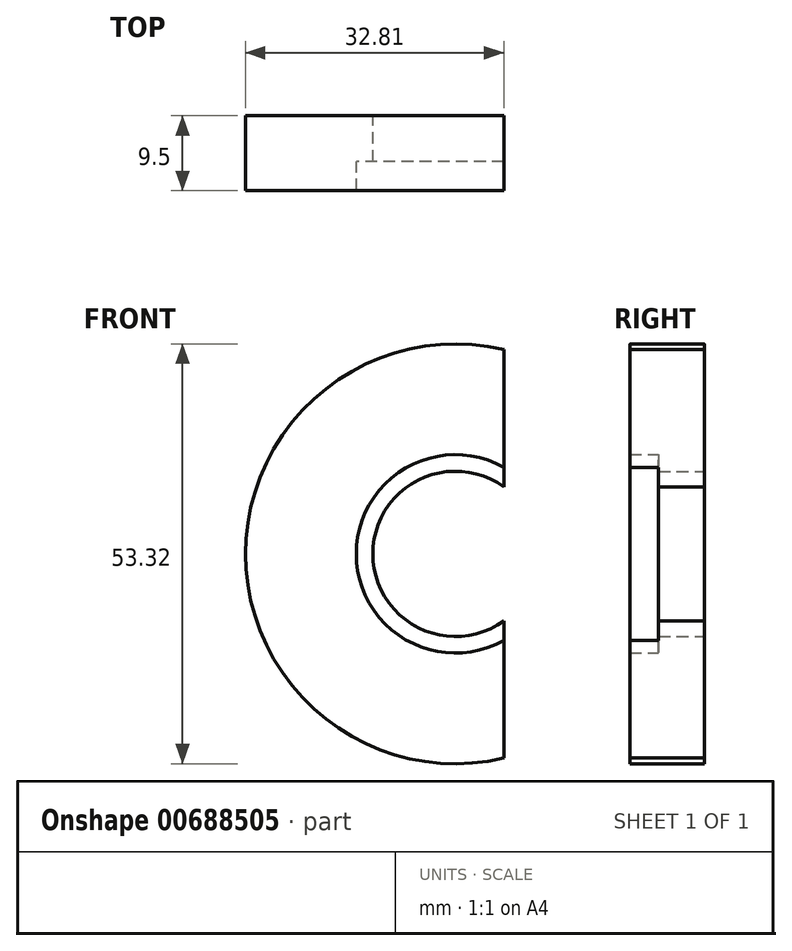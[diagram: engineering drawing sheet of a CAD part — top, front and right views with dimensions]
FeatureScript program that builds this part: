
annotation { "Feature Type Name" : "Feature", "Feature Type Description" : "" }
export const myFeature = defineFeature(function(context is Context, id is Id, definition is map)
    precondition{}
    {
        {
            var Q0;
            Q0=qCreatedBy(makeId("Top.planeOp"),FACE);
            var sketch = newSketch(context, id + "F0", { "sketchPlane" : qUnion([Q0])});
            skLineSegment(sketch, "E0", {"start": v(-57.3, 26.1) * mm, "end": v(-46.8, 26.1) * mm});
            skLineSegment(sketch, "E1", {"start": v(-57.3, 20.25) * mm, "end": v(-59.4, 20.25) * mm});
            skLineSegment(sketch, "E2", {"start": v(-59.4, 20.25) * mm, "end": v(-59.4, 16.6) * mm});
            skLineSegment(sketch, "E3", {"start": v(-46.8, 16.6) * mm, "end": v(-46.8, 10.1) * mm});
            skLineSegment(sketch, "E4", {"start": v(-65.35, 10.1) * mm, "end": v(-65.35, 16.6) * mm});
            skLineSegment(sketch, "E5", {"start": v(-65.35, 16.6) * mm, "end": v(-59.4, 16.6) * mm});
            skLineSegment(sketch, "E6", {"start": v(-57.3, 26.1) * mm, "end": v(-57.3, 20.25) * mm});
            skLineSegment(sketch, "E7", {"start": v(-46.8, 16.6) * mm, "end": v(-46.8, 20.25) * mm});
            skLineSegment(sketch, "E8", {"start": v(-46.8, 10.1) * mm, "end": v(-46.8, -14.9) * mm});
            skLineSegment(sketch, "E9", {"start": v(-68.2, -14.9) * mm, "end": v(-68.2, 10.1) * mm});
            skLineSegment(sketch, "E10", {"start": v(-68.2, 10.1) * mm, "end": v(-65.35, 10.1) * mm});
            skLineSegment(sketch, "E11", {"start": v(-46.8, -29.9) * mm, "end": v(-73.8, -29.9) * mm});
            skLineSegment(sketch, "E12", {"start": v(-73.8, -29.9) * mm, "end": v(-73.8, -14.9) * mm});
            skLineSegment(sketch, "E13", {"start": v(-73.8, -14.9) * mm, "end": v(-68.2, -14.9) * mm});
            skLineSegment(sketch, "E14", {"start": v(36.56, 75.99) * mm, "end": v(47.06, 75.99) * mm});
            skLineSegment(sketch, "E15", {"start": v(36.56, 70.14) * mm, "end": v(34.46, 70.14) * mm});
            skLineSegment(sketch, "E16", {"start": v(34.46, 70.14) * mm, "end": v(34.46, 66.49) * mm});
            skLineSegment(sketch, "E17", {"start": v(47.06, 66.49) * mm, "end": v(47.06, 59.99) * mm});
            skLineSegment(sketch, "E18", {"start": v(28.4, 59.99) * mm, "end": v(28.4, 66.49) * mm});
            skLineSegment(sketch, "E19", {"start": v(28.4, 66.49) * mm, "end": v(34.46, 66.49) * mm});
            skLineSegment(sketch, "E20", {"start": v(36.56, 75.99) * mm, "end": v(36.56, 70.14) * mm});
            skLineSegment(sketch, "E21", {"start": v(47.06, 66.49) * mm, "end": v(47.06, 70.14) * mm});
            skLineSegment(sketch, "E22", {"start": v(47.06, 59.99) * mm, "end": v(47.06, 34.99) * mm});
            skLineSegment(sketch, "E23", {"start": v(25.55, 34.99) * mm, "end": v(25.55, 59.99) * mm});
            skLineSegment(sketch, "E24", {"start": v(25.55, 59.99) * mm, "end": v(28.4, 59.99) * mm});
            skLineSegment(sketch, "E25", {"start": v(46.95, 19.99) * mm, "end": v(19.95, 19.99) * mm});
            skLineSegment(sketch, "E26", {"start": v(19.95, 19.99) * mm, "end": v(19.95, 34.99) * mm});
            skLineSegment(sketch, "E27", {"start": v(19.95, 34.99) * mm, "end": v(25.55, 34.99) * mm});
            skLineSegment(sketch, "E28", {"start": v(28.4, 66.49) * mm, "end": v(20.4, 66.49) * mm});
            skLineSegment(sketch, "E29", {"start": v(20.4, 66.49) * mm, "end": v(20.4, 75.99) * mm});
            skLineSegment(sketch, "E30", {"start": v(20.4, 75.99) * mm, "end": v(36.56, 75.99) * mm});
            skSolve(sketch);
        }
        {
            var Q0;
            Q0=sQuery(id+"F0.wireOp",EDGE,"E13");
            var Q1;
            Q1=sQuery(id+"F0.wireOp",EDGE,"E12");
            var Q2;
            Q2=sQuery(id+"F0.wireOp",EDGE,"E10");
            var Q3;
            Q3=sQuery(id+"F0.wireOp",EDGE,"E11");
            var Q4;
            Q4=sQuery(id+"F0.wireOp",EDGE,"E5");
            var Q5;
            Q5=sQuery(id+"F0.wireOp",EDGE,"E9");
            var Q6;
            Q6=sQuery(id+"F0.wireOp",EDGE,"E4");
            var Q7;
            Q7=sQuery(id+"F0.wireOp",EDGE,"E6");
            var Q8;
            Q8=sQuery(id+"F0.wireOp",EDGE,"E0");
            var Q9;
            Q9=sQuery(id+"F0.wireOp",EDGE,"E2");
            var Q10;
            Q10=sQuery(id+"F0.wireOp",EDGE,"E1");
            var Q11;
            Q11=sQuery(id+"F0.wireOp",EDGE,"E8");
            revolve(context, id + "F1", {"bodyType" : ToolBodyType.SURFACE, "surfaceEntities" : qUnion([Q0, Q1, Q2, Q3, Q4, Q5, Q6, Q7, Q8, Q9, Q10]), "axis" : qUnion([Q11]), "revolveType" : RevolveType.FULL});
        }
        {
            var Q0;
            Q0=makeQuery(id+"F1.opRevolve","SWEPT_EDGE",EDGE,{"disambiguationData":[OSD([sQuery(id+"F0.wireOp",VERTEX,"E12.end")])]});
            chamfer(context, id + "F2", {"entities" : qUnion([Q0]), "width" : 5.3 * mm, "tangentPropagation" : true});
        }
        {
            var Q0;
            Q0=makeQuery(id+"F1.opRevolve","SWEPT_EDGE",EDGE,{"disambiguationData":[OSD([sQuery(id+"F0.wireOp",VERTEX,"E0.start")])]});
            chamfer(context, id + "F3", {"entities" : qUnion([Q0]), "width" : 2 * mm, "tangentPropagation" : true});
        }
        {
            var Q0;
            Q0=makeQuery(id+"F0.imprint","IMPRINT",FACE,{"disambiguationData":[TD([[makeQuery(id+"F0.imprint","IMPRINT",EDGE,{"derivedFrom":sQuery(id+"F0.wireOp",EDGE,"E15")}),-1.0]])]});
            var Q1;
            Q1=sQuery(id+"F0.wireOp",EDGE,"E22");
            revolve(context, id + "F4", {"entities" : qUnion([Q0]), "axis" : qUnion([Q1]), "revolveType" : RevolveType.FULL});
        }
        {
            var Q0;
            Q0=makeQuery(id+"F4.opRevolve","SWEPT_FACE",FACE,{"disambiguationData":[OSD([sQuery(id+"F0.wireOp",EDGE,"E30")])]});
            var sketch = newSketch(context, id + "F5", { "sketchPlane" : qUnion([Q0])});
            skCircle(sketch, "E31.0.0", {"center": v(-47.06, 0) * mm, "radius": 26.66 * mm});
            skLineSegment(sketch, "E32", {"start": v(-53.21, 25.94) * mm, "end": v(-53.21, -25.94) * mm});
            skSolve(sketch);
        }
        {
            var Q0;
            {var subQ0=sQuery(id+"F5.wireOp",EDGE,"E32");var subQ1=sQuery(id+"F5.wireOp",EDGE,"E31.0.0");var subQ2=makeQuery(id+"F5.imprint","INTERSECT",VERTEX,{"disambiguationData":[OD(0.0)],"derivedFrom":[subQ1,subQ0]});Q0=makeQuery(id+"F5.imprint","IMPRINT",FACE,{"disambiguationData":[TD([[makeQuery(id+"F5.imprint","IMPRINT",EDGE,{"disambiguationData":[TD([[subQ2,-1.0]])],"derivedFrom":subQ1}),1.0]])]});}
            extrude(context, id + "F6", {"entities" : qUnion([Q0]), "operationType" : NewBodyOperationType.REMOVE, "endBound" : BoundingType.THROUGH_ALL, "oppositeDirection" : true, "depth" : 25 * mm, "offsetDistance" : 25 * mm});
        }
    });
